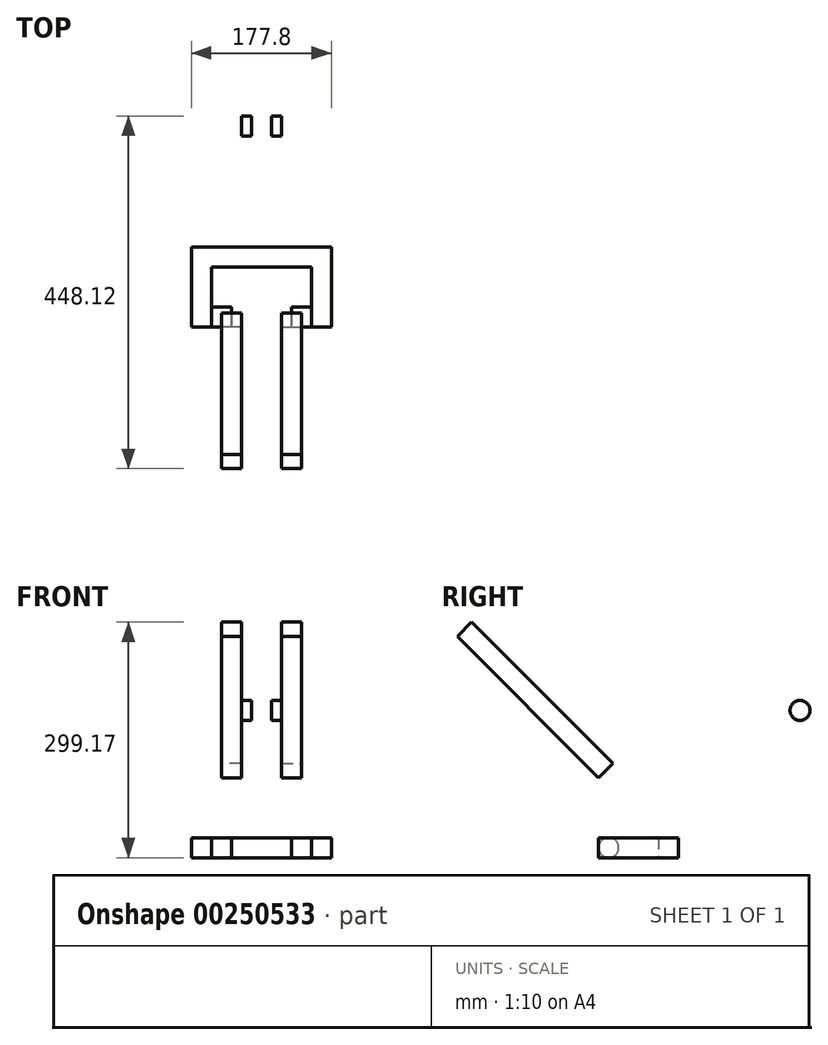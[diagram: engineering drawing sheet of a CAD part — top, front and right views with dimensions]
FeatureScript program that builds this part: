
annotation { "Feature Type Name" : "Feature", "Feature Type Description" : "" }
export const myFeature = defineFeature(function(context is Context, id is Id, definition is map)
    precondition{}
    {
        {
            var Q0;
            Q0=qCreatedBy(makeId("Top.planeOp"),FACE);
            var sketch = newSketch(context, id + "F0", { "sketchPlane" : qUnion([Q0])});
            skLineSegment(sketch, "E0", {"start": v(-63.5, 0) * mm, "end": v(-63.5, 76.2) * mm});
            skLineSegment(sketch, "E1", {"start": v(-63.5, 76.2) * mm, "end": v(0, 76.2) * mm});
            skLineSegment(sketch, "E2", {"start": v(-63.5, 0) * mm, "end": v(-88.9, 0) * mm});
            skLineSegment(sketch, "E3", {"start": v(-88.9, 0) * mm, "end": v(-88.9, 101.6) * mm});
            skLineSegment(sketch, "E4", {"start": v(-88.9, 101.6) * mm, "end": v(0, 101.6) * mm});
            skLineSegment(sketch, "E5", {"start": v(0, 167.67) * mm, "end": v(0, -61.36) * mm, "construction": true});
            skLineSegment(sketch, "E6.MirrorCS", {"start": v(88.9, 101.6) * mm, "end": v(0, 101.6) * mm});
            skLineSegment(sketch, "E7.MirrorCS", {"start": v(88.9, 0) * mm, "end": v(88.9, 101.6) * mm});
            skLineSegment(sketch, "E8.MirrorCS", {"start": v(63.5, 0) * mm, "end": v(88.9, 0) * mm});
            skLineSegment(sketch, "E9.MirrorCS", {"start": v(63.5, 0) * mm, "end": v(63.5, 76.2) * mm});
            skLineSegment(sketch, "E10.MirrorCS", {"start": v(63.5, 76.2) * mm, "end": v(0, 76.2) * mm});
            skSolve(sketch);
        }
        {
            var Q0;
            Q0=makeQuery(id+"F0.imprint","IMPRINT",FACE,{"disambiguationData":[TD([[makeQuery(id+"F0.imprint","IMPRINT",EDGE,{"derivedFrom":sQuery(id+"F0.wireOp",EDGE,"E0")}),1.0]])]});
            extrude(context, id + "F1", {"entities" : qUnion([Q0]), "depth" : 25.4 * mm});
        }
        {
            var Q0;
            Q0=makeQuery(id+"F1.opExtrude","SWEPT_FACE",FACE,{"disambiguationData":[OSD([sQuery(id+"F0.wireOp",EDGE,"E0")])]});
            var sketch = newSketch(context, id + "F2", { "sketchPlane" : qUnion([Q0])});
            skCircle(sketch, "E11", {"center": v(12.7, 12.7) * mm, "radius": 12.7 * mm});
            skSolve(sketch);
        }
        {
            var Q0;
            Q0 = qSketchRegion(id + "F2", true);
            extrude(context, id + "F3", {"entities" : qUnion([Q0]), "depth" : 25.4 * mm});
        }
        {
            var Q0;
            Q0=makeQuery(id+"F3.opExtrude","SWEPT_BODY",BODY,{"disambiguationData":[OSD([sQuery(id+"F2.wireOp",EDGE,"E11")])]});
            var Q1;
            Q1=qCreatedBy(makeId("Right.planeOp"),FACE);
            mirror(context, id + "F4", {"operationType" : NewBodyOperationType.ADD, "entities" : qUnion([Q0]), "mirrorPlane" : qUnion([Q1])});
        }
        {
            var Q0;
            Q0=qCreatedBy(makeId("Front.planeOp"),FACE);
            var Q1;
            Q1=makeQuery(id+"F1.opExtrude","CAP_EDGE",EDGE,{"disambiguationData":[OSD([sQuery(id+"F0.wireOp",EDGE,"E1"),sQuery(id+"F0.wireOp",EDGE,"E10.MirrorCS")])],"isStart":false});
            cPlane(context, id + "F5", {"entities" : qUnion([Q0, Q1]), "cplaneType" : CPlaneType.LINE_ANGLE, "offset" : 25.4 * mm, "angle" : 45 * degree, "width" : 152.4 * mm, "height" : 152.4 * mm});
        }
        {
            var Q0;
            Q0=qCreatedBy(id+"F5.planeOp",FACE);
            var sketch = newSketch(context, id + "F6", { "sketchPlane" : qUnion([Q0])});
            skLineSegment(sketch, "E12.bottom", {"start": v(25.4, 71.84) * mm, "end": v(50.8, 71.84) * mm});
            skLineSegment(sketch, "E12.top", {"start": v(25.4, 325.84) * mm, "end": v(50.8, 325.84) * mm});
            skLineSegment(sketch, "E12.left", {"start": v(25.4, 71.84) * mm, "end": v(25.4, 325.84) * mm});
            skLineSegment(sketch, "E12.right", {"start": v(50.8, 71.84) * mm, "end": v(50.8, 325.84) * mm});
            skSolve(sketch);
        }
        {
            var Q0;
            Q0 = qSketchRegion(id + "F6", true);
            extrude(context, id + "F7", {"entities" : qUnion([Q0]), "depth" : 25.4 * mm});
        }
        {
            var Q0;
            Q0=makeQuery(id+"F7.opExtrude","SWEPT_FACE",FACE,{"disambiguationData":[OSD([sQuery(id+"F6.wireOp",EDGE,"E12.left")])]});
            var sketch = newSketch(context, id + "F8", { "sketchPlane" : qUnion([Q0])});
            skCircle(sketch, "E13", {"center": v(255.8, 187.04) * mm, "radius": 12.7 * mm});
            skSolve(sketch);
        }
        {
            var Q0;
            {var subQ0=sQuery(id+"F8.wireOp",EDGE,"E13");var subQ1=sQuery(id+"F6.wireOp",EDGE,"E12.left");var subQ2=makeQuery(id+"F8.imprint","INTERSECT",VERTEX,{"derivedFrom":[makeQuery(id+"F7.opExtrude","CAP_EDGE",EDGE,{"disambiguationData":[OSD([subQ1])],"isStart":true}),subQ0]});Q0=makeQuery(id+"F8.imprint","IMPRINT",FACE,{"disambiguationData":[TD([[makeQuery(id+"F8.imprint","IMPRINT",EDGE,{"disambiguationData":[TD([[subQ2,-1.0]])],"derivedFrom":subQ0}),1.0]])]});}
            extrude(context, id + "F9", {"entities" : qUnion([Q0]), "depth" : 12.7 * mm});
        }
        {
            var Q0;
            Q0=makeQuery(id+"F7.opExtrude","SWEPT_BODY",BODY,{"disambiguationData":[OSD([sQuery(id+"F6.wireOp",EDGE,"E12.bottom"),sQuery(id+"F6.wireOp",EDGE,"E12.top"),sQuery(id+"F6.wireOp",EDGE,"E12.left"),sQuery(id+"F6.wireOp",EDGE,"E12.right")])]});
            var Q1;
            Q1=makeQuery(id+"F9.opExtrude","SWEPT_BODY",BODY,{"disambiguationData":[OSD([sQuery(id+"F8.wireOp",EDGE,"E13")])]});
            var Q2;
            Q2=qCreatedBy(makeId("Right.planeOp"),FACE);
            mirror(context, id + "F10", {"operationType" : NewBodyOperationType.ADD, "entities" : qUnion([Q0, Q1]), "mirrorPlane" : qUnion([Q2])});
        }
    });
